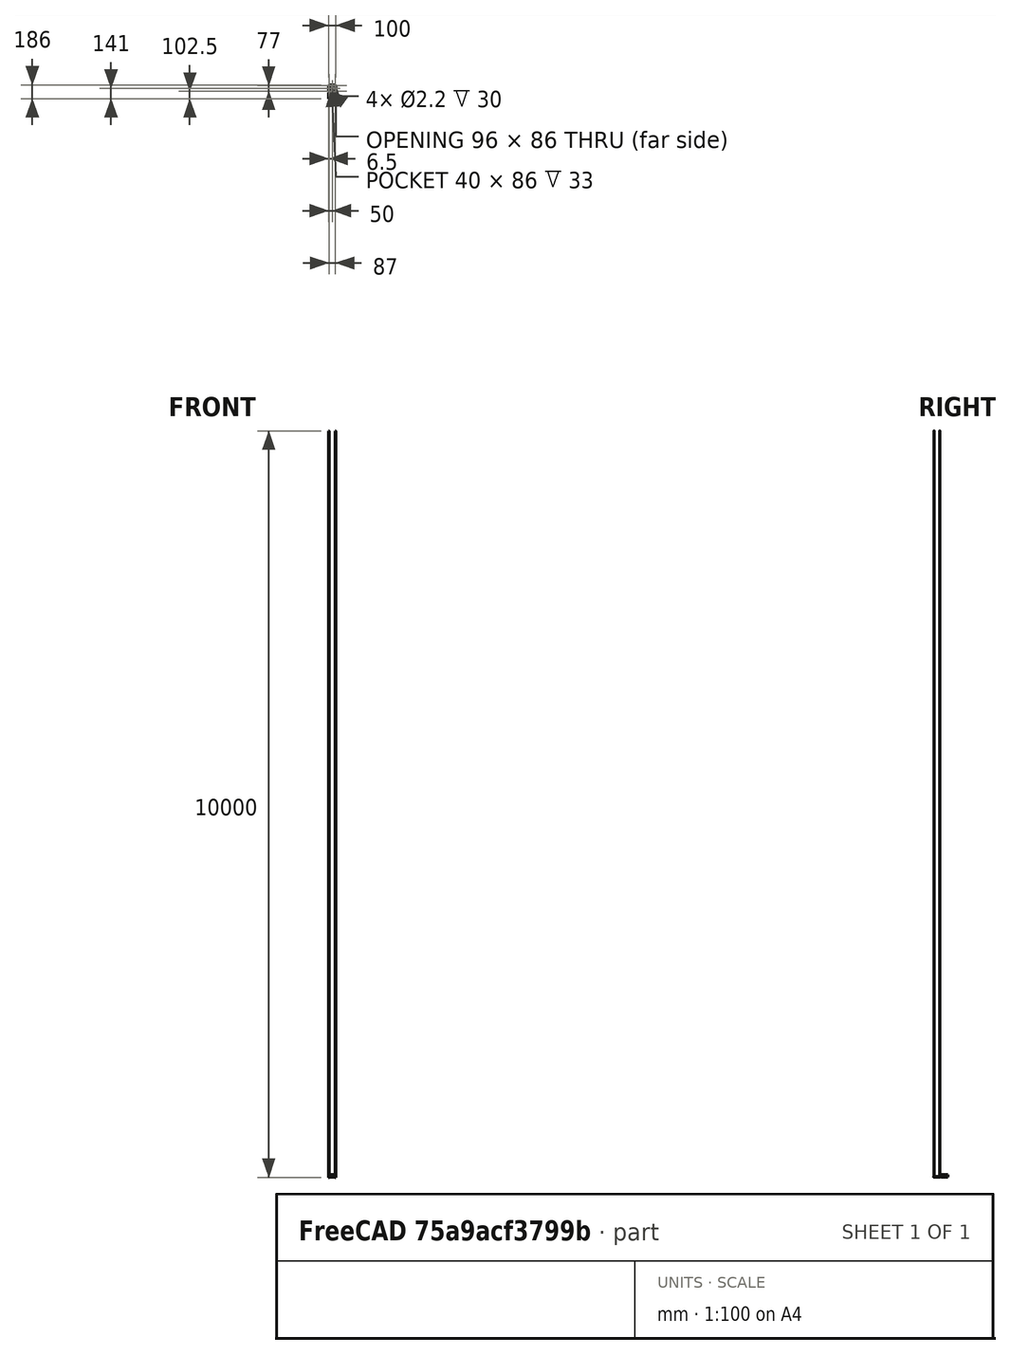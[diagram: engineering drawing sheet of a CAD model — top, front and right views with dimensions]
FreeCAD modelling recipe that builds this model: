
FCSTD DOCUMENT  (FreeCAD 0.15R4671 (Git))
Label: sensor
License: All rights reserved
LicenseURL: http://en.wikipedia.org/wiki/All_rights_reserved
objects: Sketcher::SketchObject×16, PartDesign::Pocket×11, PartDesign::Pad×5, Mesh::Feature×2
note: 48 computed .brp shape members not serialized (recipe doc carries the construction recipe); baked Part::Feature solids carry a one-line shape summary decoded from their .brp

FEATURE [Sketcher::SketchObject] Sketch  label="mainBox"
  sketch-geometry (4):
    g0: LineSegment StartX=-50 StartY=45 StartZ=0 EndX=50 EndY=45 EndZ=0
    g1: LineSegment StartX=50 StartY=45 StartZ=0 EndX=50 EndY=-45 EndZ=0
    g2: LineSegment StartX=50 StartY=-45 StartZ=0 EndX=-50 EndY=-45 EndZ=0
    g3: LineSegment StartX=-50 StartY=-45 StartZ=0 EndX=-50 EndY=45 EndZ=0
  constraints (12):
    c: Coincident(g0,g1)
    c: Coincident(g1,g2)
    c: Coincident(g2,g3)
    c: Coincident(g3,g0)
    c: Horizontal(g0)
    c: Horizontal(g2)
    c: Vertical(g1)
    c: Vertical(g3)
    c: DistanceX(g0) = 100
    c: DistanceY(g3) = 90
    c: Symmetric(g0,g2,g-1)
    c: Symmetric(g0,g0,g-2)
FEATURE [PartDesign::Pad] Pad  label="MainBox"
  Length = 35
  Length2 = 100
  Sketch = -> Sketch
  Type = 0
FEATURE [Sketcher::SketchObject] Sketch001  label="sondeTemp"
  Placement = pos=(0,0,35) rot=(0,0,1;0rad)
  Support = -> Pad [Face6]
  sketch-geometry (4):
    g0: LineSegment StartX=-48 StartY=43 StartZ=0 EndX=-8 EndY=43 EndZ=0
    g1: LineSegment StartX=-8 StartY=43 StartZ=0 EndX=-8 EndY=-43 EndZ=0
    g2: LineSegment StartX=-8 StartY=-43 StartZ=0 EndX=-48 EndY=-43 EndZ=0
    g3: LineSegment StartX=-48 StartY=-43 StartZ=0 EndX=-48 EndY=43 EndZ=0
  constraints (12):
    c: Coincident(g0,g1)
    c: Coincident(g1,g2)
    c: Coincident(g2,g3)
    c: Coincident(g3,g0)
    c: Horizontal(g0)
    c: Horizontal(g2)
    c: Vertical(g1)
    c: Vertical(g3)
    c: DistanceX(g0) = 40
    c: DistanceY(g3) = 86
    c: Symmetric(g2,g0,g-1)
    c: DistanceX(g-1,g0) = -8
FEATURE [PartDesign::Pocket] Pocket  label="tempCable"
  Length = 33
  Sketch = -> Sketch001
  Type = 0
FEATURE [Sketcher::SketchObject] Sketch002
  Placement = pos=(0,0,35) rot=(0,0,1;0rad)
  Support = -> Pocket [Face5]
  sketch-geometry (4):
    g0: LineSegment StartX=-6 StartY=43 StartZ=0 EndX=48 EndY=43 EndZ=0
    g1: LineSegment StartX=48 StartY=43 StartZ=0 EndX=48 EndY=-43 EndZ=0
    g2: LineSegment StartX=48 StartY=-43 StartZ=0 EndX=-6 EndY=-43 EndZ=0
    g3: LineSegment StartX=-6 StartY=-43 StartZ=0 EndX=-6 EndY=43 EndZ=0
  constraints (12):
    c: Coincident(g0,g1)
    c: Coincident(g1,g2)
    c: Coincident(g2,g3)
    c: Coincident(g3,g0)
    c: Horizontal(g0)
    c: Horizontal(g2)
    c: Vertical(g1)
    c: Vertical(g3)
    c: DistanceX(g0) = 54
    c: DistanceY(g1) = -86
    c: Symmetric(g0,g1,g-1)
    c: DistanceX(g-1,g0) = -6
FEATURE [PartDesign::Pocket] Pocket001  label="arduino"
  Length = 33
  Sketch = -> Sketch002
  Type = 0
FEATURE [Sketcher::SketchObject] Sketch003
  Placement = pos=(-50,0,0) rot=(0.57735,-0.57735,-0.57735;2.0944rad)
  Support = -> Pocket001 [Face2]
  sketch-geometry (1):
    g0: Circle CenterX=0 CenterY=17.5 CenterZ=0 NormalX=0 NormalY=0 NormalZ=1 Radius=3.5
  constraints (3):
    c: Radius(g0) = 3.5
    c: PointOnObject(g0,g-2)
    c: DistanceY(g-1,g0) = 17.5
FEATURE [PartDesign::Pocket] Pocket002  label="sondeTempHole"
  Length = 2
  Sketch = -> Sketch003
  Type = 0
FEATURE [Sketcher::SketchObject] Sketch004
  Placement = pos=(0,45,0) rot=(0,0.707107,0.707107;3.14159rad)
  Support = -> Pocket002 [Face1]
  sketch-geometry (4):
    g0: LineSegment StartX=-26 StartY=29 StartZ=0 EndX=-16 EndY=29 EndZ=0
    g1: LineSegment StartX=-16 StartY=29 StartZ=0 EndX=-16 EndY=19 EndZ=0
    g2: LineSegment StartX=-16 StartY=19 StartZ=0 EndX=-26 EndY=19 EndZ=0
    g3: LineSegment StartX=-26 StartY=19 StartZ=0 EndX=-26 EndY=29 EndZ=0
  constraints (12):
    c: Coincident(g0,g1)
    c: Coincident(g1,g2)
    c: Coincident(g2,g3)
    c: Coincident(g3,g0)
    c: Horizontal(g0)
    c: Horizontal(g2)
    c: Vertical(g1)
    c: Vertical(g3)
    c: DistanceX(g0) = 10
    c: DistanceY(g3) = 10
    c: DistanceY(g-1,g1) = 19
    c: DistanceX(g-1,g1) = -16
FEATURE [PartDesign::Pocket] Pocket003  label="antenna"
  Length = 2
  Sketch = -> Sketch004
  Type = 0
FEATURE [Sketcher::SketchObject] Sketch005
  Placement = pos=(50,0,0) rot=(0.57735,0.57735,0.57735;2.0944rad)
  Support = -> Pocket003 [Face5]
  sketch-geometry (5):
    g0: LineSegment StartX=-14 StartY=30 StartZ=0 EndX=-6 EndY=30 EndZ=0
    g1: LineSegment StartX=-6 StartY=30 StartZ=0 EndX=-6 EndY=26 EndZ=0
    g2: LineSegment StartX=-6 StartY=26 StartZ=0 EndX=-14 EndY=26 EndZ=0
    g3: LineSegment StartX=-14 StartY=26 StartZ=0 EndX=-14 EndY=30 EndZ=0
    g4: Circle CenterX=9 CenterY=28 CenterZ=0 NormalX=0 NormalY=0 NormalZ=1 Radius=2.5
  constraints (15):
    c: Coincident(g0,g1)
    c: Coincident(g1,g2)
    c: Coincident(g2,g3)
    c: Coincident(g3,g0)
    c: Horizontal(g0)
    c: Horizontal(g2)
    c: Vertical(g1)
    c: Vertical(g3)
    c: DistanceX(g0) = 8
    c: DistanceY(g3) = 4
    c: DistanceX(g-1,g1) = -6
    c: Radius(g4) = 2.5
    c: DistanceX(g-1,g4) = 9
    c: DistanceY(g-1,g1) = 26
    c: DistanceY(g-1,g4) = 28
FEATURE [PartDesign::Pocket] Pocket004  label="powerAndLed"
  Length = 2
  Sketch = -> Sketch005
  Type = 0
FEATURE [Sketcher::SketchObject] Sketch006
  Placement = pos=(0,0,2) rot=(0,0,1;0rad)
  Support = -> Pocket004 [Face25]
  sketch-geometry (4):
    g0: Circle CenterX=42.5 CenterY=21 CenterZ=0 NormalX=0 NormalY=0 NormalZ=1 Radius=2.5
    g1: Circle CenterX=-0.5 CenterY=21 CenterZ=0 NormalX=0 NormalY=0 NormalZ=1 Radius=2.5
    g2: Circle CenterX=-0.5 CenterY=-21 CenterZ=0 NormalX=0 NormalY=0 NormalZ=1 Radius=2.5
    g3: Circle CenterX=42.5 CenterY=-21 CenterZ=0 NormalX=0 NormalY=0 NormalZ=1 Radius=2.5
  constraints (10):
    c: Radius(g0) = 2.5
    c: DistanceX(g-1,g0) = 42.5
    c: DistanceY(g-1,g0) = 21
    c: DistanceX(g1,g0) = 43
    c: DistanceY(g0,g1) = 0
    c: Radius(g1) = 2.5
    c: Radius(g2) = 2.5
    c: Radius(g3) = 2.5
    c: Symmetric(g3,g0,g-1)
    c: Symmetric(g2,g1,g-1)
FEATURE [PartDesign::Pad] Pad001  label="footBoard"
  Length = 10
  Length2 = 100
  Sketch = -> Sketch006
  Type = 0
FEATURE [Sketcher::SketchObject] Sketch007
  Placement = pos=(0,0,12) rot=(0,0,1;0rad)
  Support = -> Pad001 [Face33]
  sketch-geometry (4):
    g0: Circle CenterX=42.5 CenterY=21 CenterZ=0 NormalX=0 NormalY=0 NormalZ=1 Radius=1.1
    g1: Circle CenterX=-0.5 CenterY=21 CenterZ=0 NormalX=0 NormalY=0 NormalZ=1 Radius=1.1
    g2: Circle CenterX=-0.5 CenterY=-21 CenterZ=0 NormalX=0 NormalY=0 NormalZ=1 Radius=1.1
    g3: Circle CenterX=42.5 CenterY=-21 CenterZ=0 NormalX=0 NormalY=0 NormalZ=1 Radius=1.1
  constraints (10):
    c: Radius(g0) = 1.1
    c: DistanceX(g-1,g0) = 42.5
    c: DistanceY(g-1,g0) = 21
    c: Radius(g1) = 1.1
    c: DistanceY(g1,g0) = 0
    c: DistanceX(g1,g0) = 43
    c: Radius(g2) = 1.1
    c: Radius(g3) = 1.1
    c: Symmetric(g2,g1,g-1)
    c: Symmetric(g3,g0,g-1)
FEATURE [PartDesign::Pocket] Pocket005  label="footBoard001"
  Length = 8
  Sketch = -> Sketch007
  Type = 0
FEATURE [Sketcher::SketchObject] Sketch008
  Placement = pos=(-6,0,0) rot=(0.57735,0.57735,0.57735;2.0944rad)
  Support = -> Pocket005 [Face14]
  sketch-geometry (1):
    g0: Circle CenterX=0 CenterY=24 CenterZ=0 NormalX=0 NormalY=0 NormalZ=1 Radius=3.5
  constraints (3):
    c: Radius(g0) = 3.5
    c: PointOnObject(g0,g-2)
    c: DistanceY(g-1,g0) = 24
FEATURE [PartDesign::Pocket] Pocket006  label="sondetemphole2"
  Length = 2
  Sketch = -> Sketch008
  Type = 0
FEATURE [Sketcher::SketchObject] Sketch009
  Placement = pos=(0,0,35) rot=(0,0,1;0rad)
  Support = -> Pocket006 [Face4]
  sketch-geometry (8):
    g0: LineSegment StartX=-8 StartY=43 StartZ=0 EndX=-6 EndY=43 EndZ=0
    g1: LineSegment StartX=-6 StartY=43 StartZ=0 EndX=-6 EndY=41 EndZ=0
    g2: LineSegment StartX=-6 StartY=41 StartZ=0 EndX=-8 EndY=41 EndZ=0
    g3: LineSegment StartX=-8 StartY=41 StartZ=0 EndX=-8 EndY=43 EndZ=0
    g4: LineSegment StartX=-8 StartY=-43 StartZ=0 EndX=-6 EndY=-43 EndZ=0
    g5: LineSegment StartX=-6 StartY=-43 StartZ=0 EndX=-6 EndY=-41 EndZ=0
    g6: LineSegment StartX=-6 StartY=-41 StartZ=0 EndX=-8 EndY=-41 EndZ=0
    g7: LineSegment StartX=-8 StartY=-41 StartZ=0 EndX=-8 EndY=-43 EndZ=0
  constraints (23):
    c: Coincident(g0,g1)
    c: Coincident(g1,g2)
    c: Coincident(g2,g3)
    c: Coincident(g3,g0)
    c: Horizontal(g0)
    c: Horizontal(g2)
    c: Vertical(g1)
    c: Vertical(g3)
    c: DistanceY(g0,g1) = -2
    c: DistanceY(g-1,g1) = 41
    c: DistanceX(g2,g1) = 2
    c: DistanceX(g-1,g1) = -6
    c: Coincident(g4,g5)
    c: Coincident(g5,g6)
    c: Coincident(g6,g7)
    c: Coincident(g7,g4)
    c: Horizontal(g4)
    c: Horizontal(g6)
    c: Vertical(g5)
    c: Vertical(g7)
    c: DistanceX(g5,g6) = -2
    c: DistanceY(g5,g4) = -2
    c: Symmetric(g5,g1,g-1)
FEATURE [PartDesign::Pocket] Pocket007  label="encocheCouvercle"
  Length = 6
  Sketch = -> Sketch009
  Type = 0
FEATURE [Sketcher::SketchObject] Sketch010
  Placement = pos=(0,0,0) rot=(1,0,0;3.14159rad)
  Support = -> Pocket007 [Face3]
  sketch-geometry (4):
    g0: Circle CenterX=-43.5 CenterY=38.5 CenterZ=0 NormalX=0 NormalY=0 NormalZ=1 Radius=2.5
    g1: Circle CenterX=43.5 CenterY=38.5 CenterZ=0 NormalX=0 NormalY=0 NormalZ=1 Radius=2.5
    g2: Circle CenterX=-43.5 CenterY=-38.5 CenterZ=0 NormalX=0 NormalY=0 NormalZ=1 Radius=2.5
    g3: Circle CenterX=43.5 CenterY=-38.5 CenterZ=0 NormalX=0 NormalY=0 NormalZ=1 Radius=2.5
  constraints (9):
    c: Radius(g0) = 2.5
    c: DistanceX(g-1,g0) = -43.5
    c: DistanceY(g-1,g0) = 38.5
    c: Radius(g1) = 2.5
    c: Radius(g2) = 2.5
    c: Radius(g3) = 2.5
    c: Symmetric(g2,g0,g-1)
    c: Symmetric(g0,g1,g-2)
    c: Symmetric(g1,g3,g-1)
FEATURE [PartDesign::Pad] Pad002  label="footTop"
  Length = 35
  Length2 = 100
  Reversed = true
  Sketch = -> Sketch010
  Type = 0
FEATURE [Sketcher::SketchObject] Sketch011
  Placement = pos=(0,0,35) rot=(0,0,1;0rad)
  Support = -> Pad002 [Face48]
  sketch-geometry (4):
    g0: Circle CenterX=-43.5 CenterY=38.5 CenterZ=0 NormalX=0 NormalY=0 NormalZ=1 Radius=1.1
    g1: Circle CenterX=43.5 CenterY=38.5 CenterZ=0 NormalX=0 NormalY=0 NormalZ=1 Radius=1.1
    g2: Circle CenterX=-43.5 CenterY=-38.5 CenterZ=0 NormalX=0 NormalY=0 NormalZ=1 Radius=1.1
    g3: Circle CenterX=43.5 CenterY=-38.5 CenterZ=0 NormalX=0 NormalY=0 NormalZ=1 Radius=1.1
  constraints (9):
    c: Radius(g0) = 1.1
    c: DistanceX(g-1,g0) = -43.5
    c: DistanceY(g-1,g0) = 38.5
    c: Radius(g1) = 1.1
    c: Radius(g2) = 1.1
    c: Radius(g3) = 1.1
    c: Symmetric(g0,g2,g-1)
    c: Symmetric(g0,g1,g-2)
    c: Symmetric(g3,g1,g-1)
FEATURE [PartDesign::Pocket] Pocket008  label="footTop2"
  Length = 30
  Sketch = -> Sketch011
  Type = 0
FEATURE [Sketcher::SketchObject] Sketch012
  Placement = pos=(0,0,0) rot=(1,0,0;3.14159rad)
  Support = -> Pocket008 [Face3]
  sketch-geometry (4):
    g0: LineSegment StartX=-50 StartY=55 StartZ=0 EndX=50 EndY=55 EndZ=0
    g1: LineSegment StartX=50 StartY=55 StartZ=0 EndX=50 EndY=145 EndZ=0
    g2: LineSegment StartX=50 StartY=145 StartZ=0 EndX=-50 EndY=145 EndZ=0
    g3: LineSegment StartX=-50 StartY=145 StartZ=0 EndX=-50 EndY=55 EndZ=0
  constraints (12):
    c: Coincident(g0,g1)
    c: Coincident(g1,g2)
    c: Coincident(g2,g3)
    c: Coincident(g3,g0)
    c: Horizontal(g0)
    c: Horizontal(g2)
    c: Vertical(g1)
    c: Vertical(g3)
    c: DistanceX(g2,g1) = 100
    c: DistanceY(g2,g0) = -90
    c: Symmetric(g2,g1,g-2)
    c: DistanceY(g-1,g0) = 55
FEATURE [PartDesign::Pad] Pad003
  Length = 2
  Length2 = 100
  Sketch = -> Sketch012
  Type = 0
FEATURE [Sketcher::SketchObject] Sketch013
  Placement = pos=(50,0,0) rot=(0.57735,0.57735,0.57735;2.0944rad)
  Support = -> Pad003 [Face5]
  sketch-geometry (4):
    g0: LineSegment StartX=-48 StartY=-57 StartZ=0 EndX=48 EndY=-57 EndZ=0
    g1: LineSegment StartX=48 StartY=-57 StartZ=0 EndX=48 EndY=-143 EndZ=0
    g2: LineSegment StartX=48 StartY=-143 StartZ=0 EndX=-48 EndY=-143 EndZ=0
    g3: LineSegment StartX=-48 StartY=-143 StartZ=0 EndX=-48 EndY=-57 EndZ=0
  constraints (12):
    c: Coincident(g0,g1)
    c: Coincident(g1,g2)
    c: Coincident(g2,g3)
    c: Coincident(g3,g0)
    c: Horizontal(g0)
    c: Horizontal(g2)
    c: Vertical(g1)
    c: Vertical(g3)
    c: DistanceX(g0,g0) = 96
    c: DistanceY(g0,g2) = -86
    c: Symmetric(g0,g0,g-2)
    c: DistanceY(g-1,g0) = -57
FEATURE [PartDesign::Pad] Pad004
  Length = 6
  Length2 = 100
  Sketch = -> Sketch013
  Type = 0
FEATURE [Sketcher::SketchObject] Sketch014
  Placement = pos=(0,0,6) rot=(0,0,1;0rad)
  Support = -> Pad004 [Face11]
  sketch-geometry (4):
    g0: LineSegment StartX=-46 StartY=-59 StartZ=0 EndX=46 EndY=-59 EndZ=0
    g1: LineSegment StartX=46 StartY=-59 StartZ=0 EndX=46 EndY=-141 EndZ=0
    g2: LineSegment StartX=46 StartY=-141 StartZ=0 EndX=-46 EndY=-141 EndZ=0
    g3: LineSegment StartX=-46 StartY=-141 StartZ=0 EndX=-46 EndY=-59 EndZ=0
  constraints (12):
    c: Coincident(g0,g1)
    c: Coincident(g1,g2)
    c: Coincident(g2,g3)
    c: Coincident(g3,g0)
    c: Horizontal(g0)
    c: Horizontal(g2)
    c: Vertical(g1)
    c: Vertical(g3)
    c: DistanceY(g0,g1) = -82
    c: DistanceX(g0,g0) = 92
    c: Symmetric(g0,g0,g-2)
    c: DistanceY(g-1,g0) = -59
FEATURE [PartDesign::Pocket] Pocket009
  Length = 6
  Sketch = -> Sketch014
  Type = 0
FEATURE [Sketcher::SketchObject] Sketch015
  Placement = pos=(0,0,-2) rot=(1,0,0;3.14159rad)
  Support = -> Pocket009 [Face5]
  sketch-geometry (4):
    g0: Circle CenterX=-43.5 CenterY=138.5 CenterZ=0 NormalX=0 NormalY=0 NormalZ=1 Radius=1.5
    g1: Circle CenterX=-43.5 CenterY=61.5 CenterZ=0 NormalX=0 NormalY=0 NormalZ=1 Radius=1.5
    g2: Circle CenterX=43.5 CenterY=138.5 CenterZ=0 NormalX=0 NormalY=0 NormalZ=1 Radius=1.5
    g3: Circle CenterX=43.5 CenterY=61.5 CenterZ=0 NormalX=0 NormalY=0 NormalZ=1 Radius=1.5
  constraints (10):
    c: Radius(g0) = 1.5
    c: Radius(g1) = 1.5
    c: Radius(g2) = 1.5
    c: Radius(g3) = 1.5
    c: DistanceX(g-1,g0) = -43.5
    c: DistanceY(g-1,g0) = 138.5
    c: DistanceY(g-1,g1) = 61.5
    c: DistanceX(g-1,g1) = -43.5
    c: Symmetric(g1,g3,g-2)
    c: Symmetric(g0,g2,g-2)
FEATURE [PartDesign::Pocket] Pocket010
  Length = 5
  Sketch = -> Sketch015
  Type = 1
FEATURE [Mesh::Feature] Mesh  label="footTop2 (Meshed)"
FEATURE [Mesh::Feature] Mesh001  label="Pocket010 (Meshed)"
